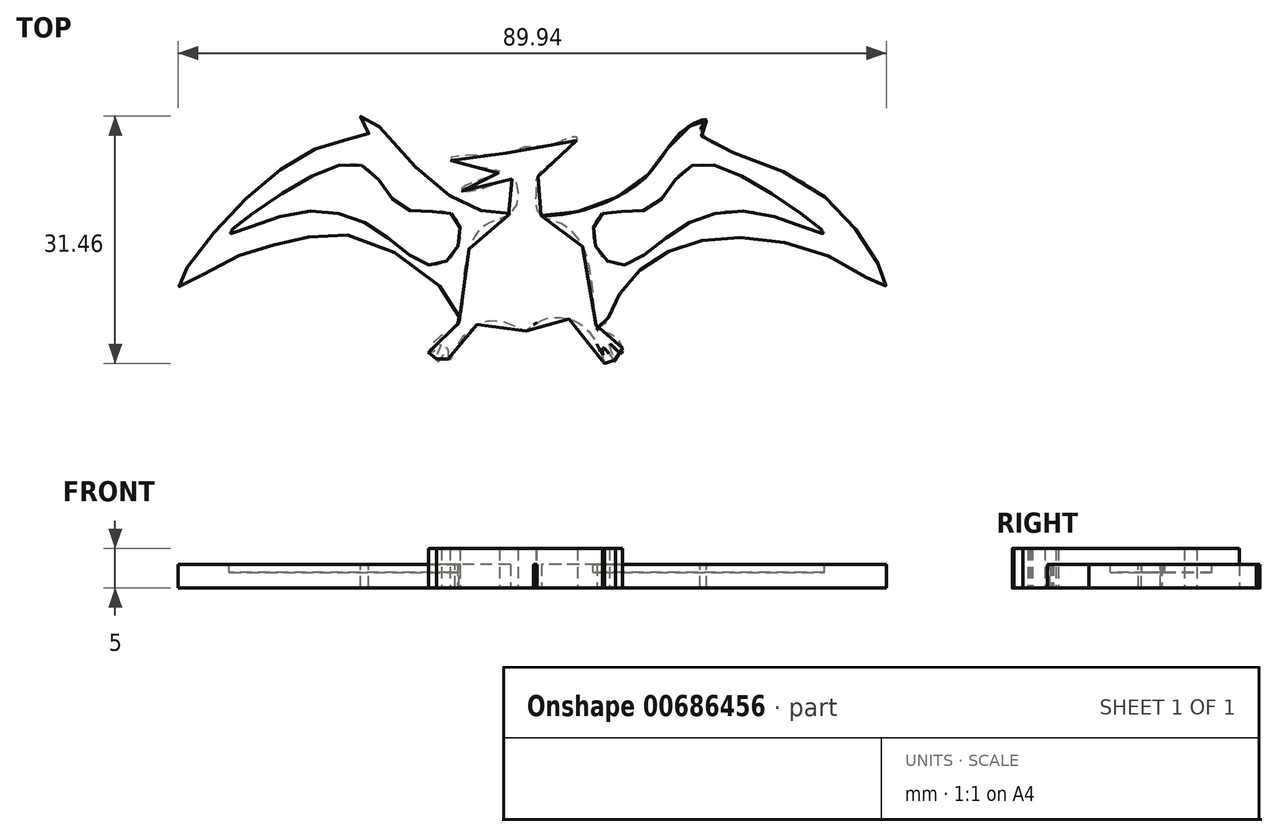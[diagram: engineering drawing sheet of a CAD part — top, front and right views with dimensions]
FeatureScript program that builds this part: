
annotation { "Feature Type Name" : "Feature", "Feature Type Description" : "" }
export const myFeature = defineFeature(function(context is Context, id is Id, definition is map)
    precondition{}
    {
        {
            var Q0;
            Q0=qCreatedBy(makeId("Top.planeOp"),FACE);
            var sketch = newSketch(context, id + "F0", { "sketchPlane" : qUnion([Q0])});
            skFitSpline(sketch, "E0", {"points": [v(27.34, -13.6) * mm, v(24.03, -13.84) * mm, v(21.92, -14.57) * mm, v(14.89, -15.14) * mm, v(15.7, -15.78) * mm, v(21.11, -16.83) * mm, v(18.37, -18.05) * mm, v(16.1, -19.26) * mm, v(19.17, -19.02) * mm, v(22.73, -17.89) * mm, v(23.46, -19.66) * mm, v(22.49, -22.25) * mm, v(19.17, -23.79) * mm, v(16.67, -29.37) * mm, v(15.62, -36.73) * mm, v(13.03, -38.18) * mm, v(12.22, -40.04) * mm, v(13.76, -38.75) * mm, v(13.1, -40.36) * mm, v(13.43, -41.1) * mm, v(14.48, -39.07) * mm, v(14.65, -41.1) * mm, v(15.94, -38.67) * mm, v(20.8, -35.75) * mm, v(24.35, -37.13) * mm, v(24.67, -36.97) * mm, v(27.02, -35.6) * mm, v(32.6, -37.37) * mm, v(34.46, -41.25) * mm, v(34.3, -39.31) * mm, v(35.83, -41.1) * mm, v(35.1, -38.83) * mm, v(36.56, -39.96) * mm, v(36.32, -38.42) * mm, v(34.05, -37.21) * mm, v(33.49, -36.8) * mm, v(32.27, -27.91) * mm, v(28.8, -23.46) * mm, v(26.13, -22.17) * mm, v(25.8, -19.34) * mm, v(26.05, -17.4) * mm, v(29.44, -14.4) * mm, v(30.98, -12.55) * mm, v(29.44, -12.8) * mm, v(27.34, -13.6) * mm]});
            skSolve(sketch);
        }
        {
            var Q0;
            Q0 = qSketchRegion(id + "F0", true);
            extrude(context, id + "F1", {"entities" : qUnion([Q0]), "depth" : 5 * mm, "offsetDistance" : 25 * mm});
        }
        {
            var Q0;
            Q0=qCreatedBy(makeId("Top.planeOp"),FACE);
            var sketch = newSketch(context, id + "F2", { "sketchPlane" : qUnion([Q0])});
            skLineSegment(sketch, "E1", {"start": v(25.2, 12.88) * mm, "end": v(25.2, -63.65) * mm});
            skFitSpline(sketch, "E2", {"points": [v(22.12, -22.22) * mm, v(16.18, -20.85) * mm, v(8.06, -13.76) * mm, v(6.23, -11.48) * mm, v(3.48, -9.88) * mm, v(4.51, -12.05) * mm, v(1.43, -12.85) * mm, v(-6.92, -16.85) * mm, v(-16.76, -26.57) * mm, v(-19.61, -31.49) * mm, v(-14.01, -28.51) * mm, v(-5.55, -25.77) * mm, v(4.51, -25.65) * mm, v(15.95, -35.15) * mm, v(15.49, -36.52) * mm, v(18.46, -35.37) * mm, v(23.6, -35.15) * mm, v(25.2, -36.4) * mm, v(28.07, -34.8) * mm, v(33.1, -36.75) * mm, v(34.59, -36.17) * mm, v(36.3, -32.52) * mm, v(41.68, -27.48) * mm, v(50.37, -25.31) * mm, v(63.74, -28.06) * mm, v(70.15, -31.49) * mm, v(67.98, -26.57) * mm, v(57.57, -17.08) * mm, v(46.6, -11.93) * mm, v(47.4, -10.33) * mm, v(44.3, -11.82) * mm, v(39.73, -17.54) * mm, v(29.78, -22.22) * mm, v(22.12, -22.22) * mm]});
            skSolve(sketch);
        }
        {
            var Q0;
            Q0 = qSketchRegion(id + "F2", true);
            extrude(context, id + "F3", {"entities" : qUnion([Q0]), "operationType" : NewBodyOperationType.ADD, "depth" : 3 * mm, "offsetDistance" : 25 * mm});
        }
        {
            var Q0;
            Q0=makeQuery(id+"F3.boolean.opBoolean","SPLIT",FACE,{"disambiguationData":[OD(0.0)],"derivedFrom":makeQuery(id+"F3.opExtrude","CAP_FACE",FACE,{"disambiguationData":[OSD([sQuery(id+"F2.wireOp",EDGE,"E2")])],"isStart":false})});
            var sketch = newSketch(context, id + "F4", { "sketchPlane" : qUnion([Q0])});
            skFitSpline(sketch, "E3", {"points": [v(14.96, -22.25) * mm, v(9.01, -21.61) * mm, v(4.11, -16.36) * mm, v(-5.68, -19.16) * mm, v(-13.23, -24.78) * mm, v(-5.35, -22.25) * mm, v(5.29, -24.17) * mm, v(12.63, -28.8) * mm, v(15.98, -26.03) * mm, v(14.96, -22.25) * mm]});
            skLineSegment(sketch, "E4", {"start": v(24.59, -37.19) * mm, "end": v(24.59, -13.74) * mm});
            skFitSpline(sketch, "E5.MirrorC", {"points": [v(34.21, -22.25) * mm, v(40.16, -21.61) * mm, v(45.06, -16.36) * mm, v(54.86, -19.16) * mm, v(62.4, -24.78) * mm, v(54.52, -22.25) * mm, v(43.89, -24.17) * mm, v(36.54, -28.8) * mm, v(33.2, -26.03) * mm, v(34.21, -22.25) * mm]});
            skSolve(sketch);
        }
        {
            var Q0;
            Q0 = qSketchRegion(id + "F4", true);
            extrude(context, id + "F5", {"entities" : qUnion([Q0]), "operationType" : NewBodyOperationType.REMOVE, "oppositeDirection" : true, "depth" : 1 * mm, "offsetDistance" : 25 * mm});
        }
    });
